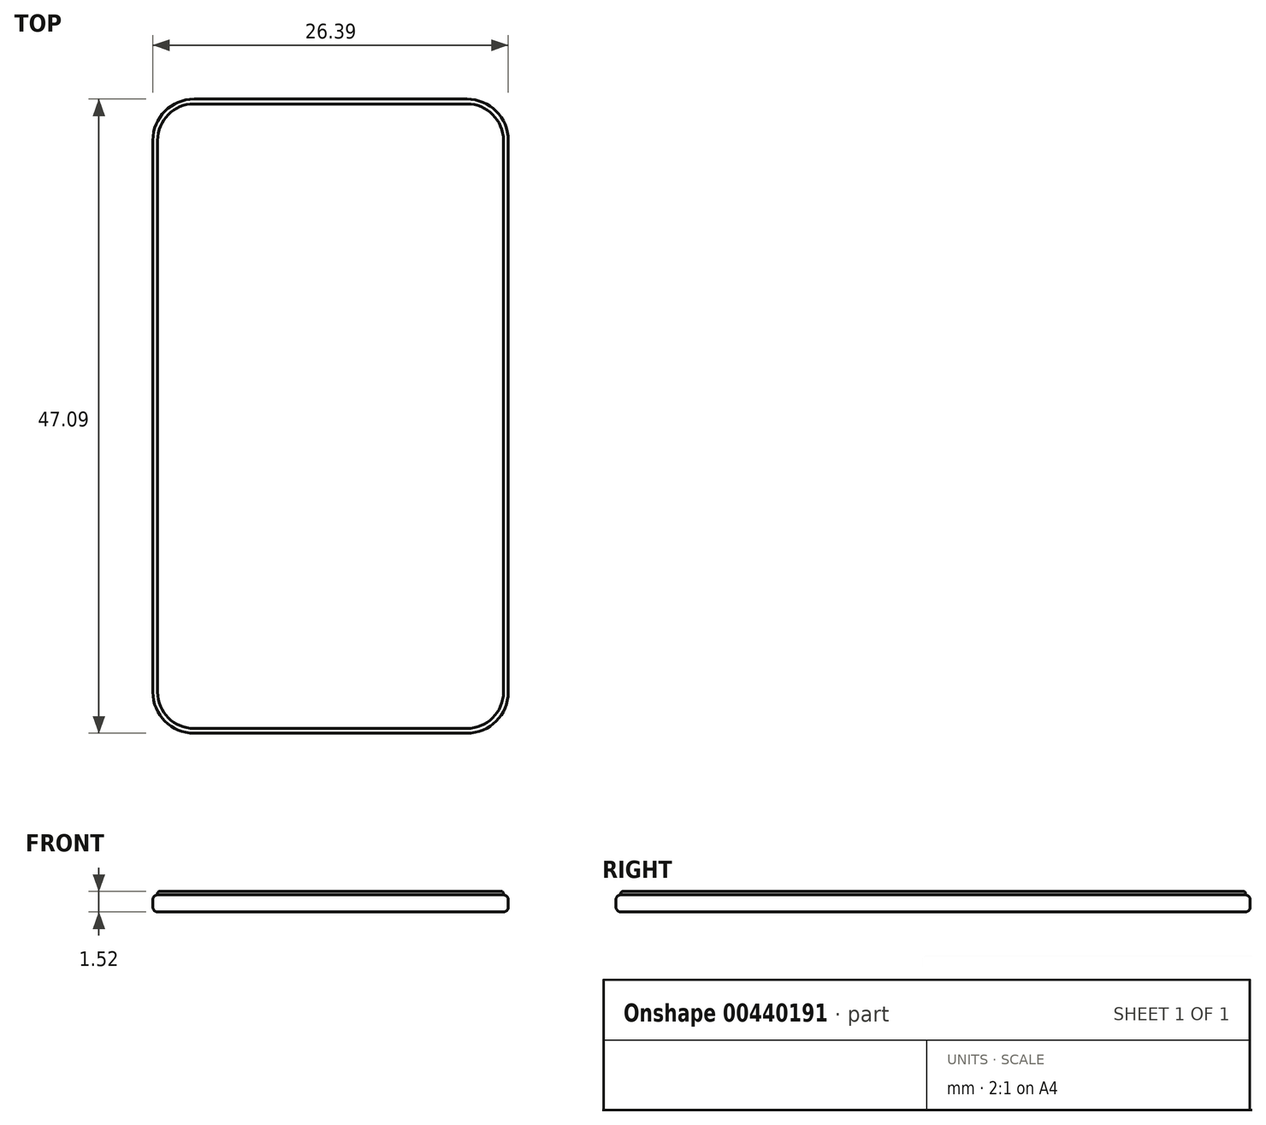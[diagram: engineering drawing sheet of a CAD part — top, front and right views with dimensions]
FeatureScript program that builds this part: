
annotation { "Feature Type Name" : "Feature", "Feature Type Description" : "" }
export const myFeature = defineFeature(function(context is Context, id is Id, definition is map)
    precondition{}
    {
        {
            var Q0;
            Q0=qCreatedBy(makeId("Top.planeOp"),FACE);
            var sketch = newSketch(context, id + "F0", { "sketchPlane" : qUnion([Q0])});
            skLineSegment(sketch, "E0.bottom", {"start": v(0, 0) * mm, "end": v(26.39, 0) * mm});
            skLineSegment(sketch, "E0.top", {"start": v(0, 47.09) * mm, "end": v(26.39, 47.09) * mm});
            skLineSegment(sketch, "E0.left", {"start": v(0, 0) * mm, "end": v(0, 47.09) * mm});
            skLineSegment(sketch, "E0.right", {"start": v(26.39, 0) * mm, "end": v(26.39, 47.09) * mm});
            skSolve(sketch);
        }
        {
            var Q0;
            Q0 = qSketchRegion(id + "F0", true);
            extrude(context, id + "F1", {"entities" : qUnion([Q0]), "depth" : 1.27 * mm});
        }
        {
            var Q0;
            Q0=makeQuery(id+"F1.opExtrude","SWEPT_EDGE",EDGE,{"disambiguationData":[OSD([sQuery(id+"F0.wireOp",EDGE,"E0.top"),sQuery(id+"F0.wireOp",EDGE,"E0.right")])]});
            var Q1;
            Q1=makeQuery(id+"F1.opExtrude","SWEPT_EDGE",EDGE,{"disambiguationData":[OSD([sQuery(id+"F0.wireOp",EDGE,"E0.bottom"),sQuery(id+"F0.wireOp",EDGE,"E0.right")])]});
            var Q2;
            Q2=makeQuery(id+"F1.opExtrude","SWEPT_EDGE",EDGE,{"disambiguationData":[OSD([sQuery(id+"F0.wireOp",EDGE,"E0.top"),sQuery(id+"F0.wireOp",EDGE,"E0.left")])]});
            var Q3;
            Q3=makeQuery(id+"F1.opExtrude","SWEPT_EDGE",EDGE,{"disambiguationData":[OSD([sQuery(id+"F0.wireOp",EDGE,"E0.bottom"),sQuery(id+"F0.wireOp",EDGE,"E0.left")])]});
            fillet(context, id + "F2", {"entities" : qUnion([Q0, Q1, Q2, Q3]), "radius" : 3.07 * mm, "tangentPropagation" : true, "allowEdgeOverflow" : false});
        }
        {
            var Q0;
            Q0=makeQuery(id+"F1.opExtrude","CAP_FACE",FACE,{"disambiguationData":[OSD([sQuery(id+"F0.wireOp",EDGE,"E0.bottom"),sQuery(id+"F0.wireOp",EDGE,"E0.top"),sQuery(id+"F0.wireOp",EDGE,"E0.left"),sQuery(id+"F0.wireOp",EDGE,"E0.right")])],"isStart":true});
            fillet(context, id + "F3", {"entities" : qUnion([Q0]), "radius" : 0.36 * mm, "tangentPropagation" : true, "allowEdgeOverflow" : false});
        }
        {
            var Q0;
            Q0=makeQuery(id+"F1.opExtrude","CAP_FACE",FACE,{"disambiguationData":[OSD([sQuery(id+"F0.wireOp",EDGE,"E0.bottom"),sQuery(id+"F0.wireOp",EDGE,"E0.top"),sQuery(id+"F0.wireOp",EDGE,"E0.left"),sQuery(id+"F0.wireOp",EDGE,"E0.right")])],"isStart":false});
            fillet(context, id + "F4", {"entities" : qUnion([Q0]), "radius" : 0.36 * mm, "tangentPropagation" : true, "allowEdgeOverflow" : false});
        }
        {
            var Q0;
            Q0=makeQuery(id+"F1.opExtrude","CAP_FACE",FACE,{"disambiguationData":[OSD([sQuery(id+"F0.wireOp",EDGE,"E0.bottom"),sQuery(id+"F0.wireOp",EDGE,"E0.top"),sQuery(id+"F0.wireOp",EDGE,"E0.left"),sQuery(id+"F0.wireOp",EDGE,"E0.right")])],"isStart":false});
            var sketch = newSketch(context, id + "F5", { "sketchPlane" : qUnion([Q0])});
            skLineSegment(sketch, "E1", {"start": v(26.03, 44.02) * mm, "end": v(26.03, 3.07) * mm});
            skLineSegment(sketch, "E2", {"start": v(23.32, 46.73) * mm, "end": v(3.07, 46.73) * mm});
            skLineSegment(sketch, "E3", {"start": v(0.36, 44.02) * mm, "end": v(0.36, 3.07) * mm});
            skLineSegment(sketch, "E4", {"start": v(3.07, 0.36) * mm, "end": v(23.32, 0.36) * mm});
            skArc(sketch, "E5", {"start": v(3.07, 46.73) * mm, "mid": v(1.15, 45.94) * mm, "end": v(0.36, 44.02) * mm});
            skArc(sketch, "E6", {"start": v(26.03, 44.02) * mm, "mid": v(25.24, 45.94) * mm, "end": v(23.32, 46.73) * mm});
            skArc(sketch, "E7", {"start": v(0.36, 3.07) * mm, "mid": v(1.15, 1.15) * mm, "end": v(3.07, 0.36) * mm});
            skArc(sketch, "E8", {"start": v(23.32, 0.36) * mm, "mid": v(25.24, 1.15) * mm, "end": v(26.03, 3.07) * mm});
            skSolve(sketch);
        }
        {
            var Q0;
            Q0=makeQuery(id+"F5.imprint","IMPRINT",FACE,{"disambiguationData":[TD([[makeQuery(id+"F5.imprint","IMPRINT",EDGE,{"derivedFrom":sQuery(id+"F5.wireOp",EDGE,"E1")}),1.0]])]});
            extrude(context, id + "F6", {"entities" : qUnion([Q0]), "operationType" : NewBodyOperationType.ADD, "depth" : 0.25 * mm});
        }
        {
            var Q0;
            Q0=makeQuery(id+"F6.opExtrude","CAP_FACE",FACE,{"disambiguationData":[OSD([sQuery(id+"F5.wireOp",EDGE,"E1"),sQuery(id+"F5.wireOp",EDGE,"E2"),sQuery(id+"F5.wireOp",EDGE,"E3"),sQuery(id+"F5.wireOp",EDGE,"E4"),sQuery(id+"F5.wireOp",EDGE,"E5"),sQuery(id+"F5.wireOp",EDGE,"E6"),sQuery(id+"F5.wireOp",EDGE,"E7"),sQuery(id+"F5.wireOp",EDGE,"E8")])],"isStart":false});
            fillet(context, id + "F7", {"entities" : qUnion([Q0]), "radius" : 0.13 * mm, "tangentPropagation" : true, "allowEdgeOverflow" : false});
        }
    });
